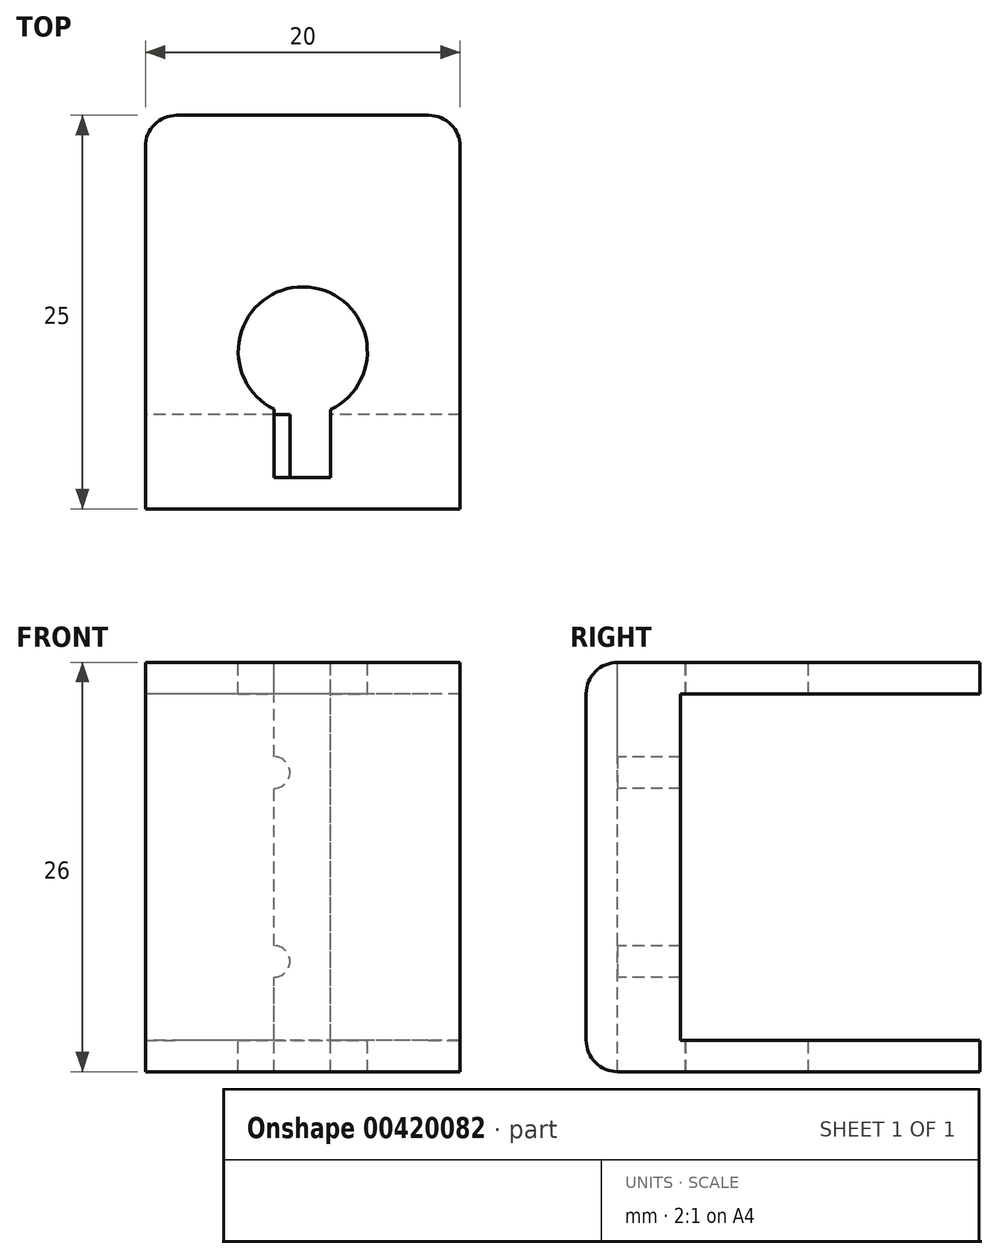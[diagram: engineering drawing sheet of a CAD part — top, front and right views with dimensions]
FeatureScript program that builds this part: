
annotation { "Feature Type Name" : "Feature", "Feature Type Description" : "" }
export const myFeature = defineFeature(function(context is Context, id is Id, definition is map)
    precondition{}
    {
        {
            var Q0;
            Q0=qCreatedBy(makeId("Right.planeOp"),FACE);
            var sketch = newSketch(context, id + "F0", { "sketchPlane" : qUnion([Q0])});
            skLineSegment(sketch, "E0", {"start": v(0, 0) * mm, "end": v(25, 0) * mm});
            skLineSegment(sketch, "E1", {"start": v(25, 0) * mm, "end": v(25, 2) * mm});
            skLineSegment(sketch, "E2", {"start": v(25, 2) * mm, "end": v(6, 2) * mm});
            skLineSegment(sketch, "E3", {"start": v(6, 2) * mm, "end": v(6, 4) * mm});
            skLineSegment(sketch, "E4", {"start": v(6, 4) * mm, "end": v(2, 4) * mm});
            skLineSegment(sketch, "E5", {"start": v(2, 4) * mm, "end": v(2, 22) * mm});
            skLineSegment(sketch, "E6", {"start": v(2, 22) * mm, "end": v(6, 22) * mm});
            skLineSegment(sketch, "E7", {"start": v(6, 22) * mm, "end": v(6, 24) * mm});
            skLineSegment(sketch, "E8", {"start": v(6, 24) * mm, "end": v(25, 24) * mm});
            skLineSegment(sketch, "E9", {"start": v(25, 24) * mm, "end": v(25, 26) * mm});
            skLineSegment(sketch, "E10", {"start": v(25, 26) * mm, "end": v(0, 26) * mm});
            skLineSegment(sketch, "E11", {"start": v(0, 26) * mm, "end": v(0, 0) * mm});
            skLineSegment(sketch, "E12", {"start": v(6, 22) * mm, "end": v(6, 4) * mm});
            skSolve(sketch);
        }
        {
            var Q0;
            Q0=makeQuery(id+"F0.imprint","IMPRINT",FACE,{"disambiguationData":[TD([[makeQuery(id+"F0.imprint","IMPRINT",EDGE,{"derivedFrom":sQuery(id+"F0.wireOp",EDGE,"hZs9axiV-JyNc-4rnQ-Btlt-CpWUZ3mN9xeb")}),-1.0]])]});
            var Q1;
            Q1=makeQuery(id+"F0.imprint","IMPRINT",FACE,{"disambiguationData":[TD([[makeQuery(id+"F0.imprint","IMPRINT",EDGE,{"derivedFrom":sQuery(id+"F0.wireOp",EDGE,"E0")}),1.0]])]});
            var Q2;
            Q2=makeQuery(id+"F0.imprint","IMPRINT",FACE,{"disambiguationData":[TD([[makeQuery(id+"F0.imprint","IMPRINT",EDGE,{"derivedFrom":sQuery(id+"F0.wireOp",EDGE,"E4")}),-1.0]])]});
            extrude(context, id + "F1", {"entities" : qUnion([Q0, Q1, Q2]), "depth" : 20 * mm});
        }
        {
            var Q0;
            Q0=makeQuery(id+"F1.opExtrude","SWEPT_FACE",FACE,{"disambiguationData":[OSD([sQuery(id+"F0.wireOp",EDGE,"E10")])]});
            var sketch = newSketch(context, id + "F2", { "sketchPlane" : qUnion([Q0])});
            skPoint(sketch, "E13", {"position": v(10, 0) * mm});
            skLineSegment(sketch, "E14", {"start": v(10, 0) * mm, "end": v(10, 2) * mm, "construction": true});
            skLineSegment(sketch, "E15", {"start": v(10, 2) * mm, "end": v(10, 10) * mm, "construction": true});
            skCircle(sketch, "E16", {"center": v(10, 10) * mm, "radius": 4.1 * mm});
            skLineSegment(sketch, "E17", {"start": v(10, 2) * mm, "end": v(11.76, 2) * mm});
            skLineSegment(sketch, "E18", {"start": v(11.76, 2) * mm, "end": v(11.76, 6.3) * mm});
            skLineSegment(sketch, "E19", {"start": v(10, 2) * mm, "end": v(8.18, 2) * mm});
            skLineSegment(sketch, "E20", {"start": v(8.18, 2) * mm, "end": v(8.18, 6.33) * mm});
            skSolve(sketch);
        }
        {
            var Q0;
            Q0=makeQuery(id+"F2.imprint","IMPRINT",FACE,{"disambiguationData":[TD([[makeQuery(id+"F2.imprint","IMPRINT",EDGE,{"derivedFrom":sQuery(id+"F2.wireOp",EDGE,"E17")}),1.0]])]});
            var Q1;
            {var subQ0=sQuery(id+"F2.wireOp",EDGE,"E16");var subQ1=makeQuery(id+"F2.imprint","INTERSECT",VERTEX,{"derivedFrom":[subQ0,sQuery(id+"F2.wireOp",EDGE,"E18")]});Q1=makeQuery(id+"F2.imprint","IMPRINT",FACE,{"disambiguationData":[TD([[makeQuery(id+"F2.imprint","IMPRINT",EDGE,{"disambiguationData":[TD([[subQ1,1.0]])],"derivedFrom":subQ0}),1.0]])]});}
            extrude(context, id + "F3", {"entities" : qUnion([Q0, Q1]), "operationType" : NewBodyOperationType.REMOVE, "oppositeDirection" : true, "depth" : 30 * mm});
        }
        {
            var Q0;
            Q0=makeQuery(id+"F3.boolean.opBoolean","COPY",FACE,{"derivedFrom":makeQuery(id+"F3.opExtrude","SWEPT_FACE",FACE,{"disambiguationData":[OSD([sQuery(id+"F2.wireOp",EDGE,"E17"),sQuery(id+"F2.wireOp",EDGE,"E19")])]})});
            var sketch = newSketch(context, id + "F4", { "sketchPlane" : qUnion([Q0])});
            skLineSegment(sketch, "E21", {"start": v(-11.76, 26) * mm, "end": v(-11.76, 13) * mm, "construction": true});
            skLineSegment(sketch, "E22", {"start": v(-11.76, 13) * mm, "end": v(-11.76, 0) * mm, "construction": true});
            skCircle(sketch, "E23", {"center": v(-11.76, 13) * mm, "radius": 1 * mm});
            skLineSegment(sketch, "E24", {"start": v(-8.18, 26) * mm, "end": v(-8.18, 19) * mm, "construction": true});
            skLineSegment(sketch, "E25", {"start": v(-8.18, 19) * mm, "end": v(-8.18, 7) * mm, "construction": true});
            skLineSegment(sketch, "E26", {"start": v(-8.18, 7) * mm, "end": v(-8.18, 0) * mm, "construction": true});
            skCircle(sketch, "E27", {"center": v(-8.18, 19) * mm, "radius": 1 * mm});
            skCircle(sketch, "E28", {"center": v(-8.18, 7) * mm, "radius": 1 * mm});
            skSolve(sketch);
        }
        {
            var Q0;
            {var subQ0=sQuery(id+"F4.wireOp",EDGE,"E27");var subQ1=makeQuery(id+"F3.boolean.opBoolean","COPY",EDGE,{"derivedFrom":makeQuery(id+"F3.opExtrude","SWEPT_EDGE",EDGE,{"disambiguationData":[OSD([sQuery(id+"F2.wireOp",EDGE,"E19"),sQuery(id+"F2.wireOp",EDGE,"E20")])]})});var subQ2=makeQuery(id+"F4.imprint","INTERSECT",VERTEX,{"disambiguationData":[OD(0.0)],"derivedFrom":[subQ1,subQ0]});Q0=makeQuery(id+"F4.imprint","IMPRINT",FACE,{"disambiguationData":[TD([[makeQuery(id+"F4.imprint","IMPRINT",EDGE,{"disambiguationData":[TD([[subQ2,-1.0]])],"derivedFrom":subQ0}),1.0]])]});}
            var Q1;
            {var subQ0=sQuery(id+"F4.wireOp",EDGE,"E23");var subQ1=makeQuery(id+"F3.boolean.opBoolean","COPY",EDGE,{"derivedFrom":makeQuery(id+"F3.opExtrude","SWEPT_EDGE",EDGE,{"disambiguationData":[OSD([sQuery(id+"F2.wireOp",EDGE,"E17"),sQuery(id+"F2.wireOp",EDGE,"E18")])]})});var subQ2=makeQuery(id+"F4.imprint","INTERSECT",VERTEX,{"disambiguationData":[OD(0.0)],"derivedFrom":[subQ1,subQ0]});Q1=makeQuery(id+"F4.imprint","IMPRINT",FACE,{"disambiguationData":[TD([[makeQuery(id+"F4.imprint","IMPRINT",EDGE,{"disambiguationData":[TD([[subQ2,1.0]])],"derivedFrom":subQ0}),1.0]])]});}
            var Q2;
            {var subQ0=sQuery(id+"F4.wireOp",EDGE,"E28");var subQ1=makeQuery(id+"F3.boolean.opBoolean","COPY",EDGE,{"derivedFrom":makeQuery(id+"F3.opExtrude","SWEPT_EDGE",EDGE,{"disambiguationData":[OSD([sQuery(id+"F2.wireOp",EDGE,"E19"),sQuery(id+"F2.wireOp",EDGE,"E20")])]})});var subQ2=makeQuery(id+"F4.imprint","INTERSECT",VERTEX,{"disambiguationData":[OD(0.0)],"derivedFrom":[subQ1,subQ0]});Q2=makeQuery(id+"F4.imprint","IMPRINT",FACE,{"disambiguationData":[TD([[makeQuery(id+"F4.imprint","IMPRINT",EDGE,{"disambiguationData":[TD([[subQ2,1.0]])],"derivedFrom":subQ0}),1.0]])]});}
            extrude(context, id + "F5", {"entities" : qUnion([Q0, Q1, Q2]), "operationType" : NewBodyOperationType.ADD, "depth" : 4 * mm});
        }
        {
            var Q0;
            Q0=makeQuery(id+"F1.opExtrude","SWEPT_EDGE",EDGE,{"disambiguationData":[OSD([sQuery(id+"F0.wireOp",EDGE,"E10"),sQuery(id+"F0.wireOp",EDGE,"E11")])]});
            var Q1;
            Q1=makeQuery(id+"F1.opExtrude","SWEPT_EDGE",EDGE,{"disambiguationData":[OSD([sQuery(id+"F0.wireOp",EDGE,"E0"),sQuery(id+"F0.wireOp",EDGE,"E11")])]});
            var Q2;
            Q2=makeQuery(id+"F1.opExtrude","CAP_EDGE",EDGE,{"disambiguationData":[OSD([sQuery(id+"F0.wireOp",EDGE,"E1")])],"isStart":false});
            var Q3;
            Q3=makeQuery(id+"F1.opExtrude","CAP_EDGE",EDGE,{"disambiguationData":[OSD([sQuery(id+"F0.wireOp",EDGE,"E1")])],"isStart":true});
            var Q4;
            Q4=makeQuery(id+"F1.opExtrude","CAP_EDGE",EDGE,{"disambiguationData":[OSD([sQuery(id+"F0.wireOp",EDGE,"E9")])],"isStart":true});
            var Q5;
            Q5=makeQuery(id+"F1.opExtrude","CAP_EDGE",EDGE,{"disambiguationData":[OSD([sQuery(id+"F0.wireOp",EDGE,"E9")])],"isStart":false});
            fillet(context, id + "F6", {"entities" : qUnion([Q0, Q1, Q2, Q3, Q4, Q5]), "radius" : 2 * mm, "tangentPropagation" : true, "allowEdgeOverflow" : false});
        }
    });
